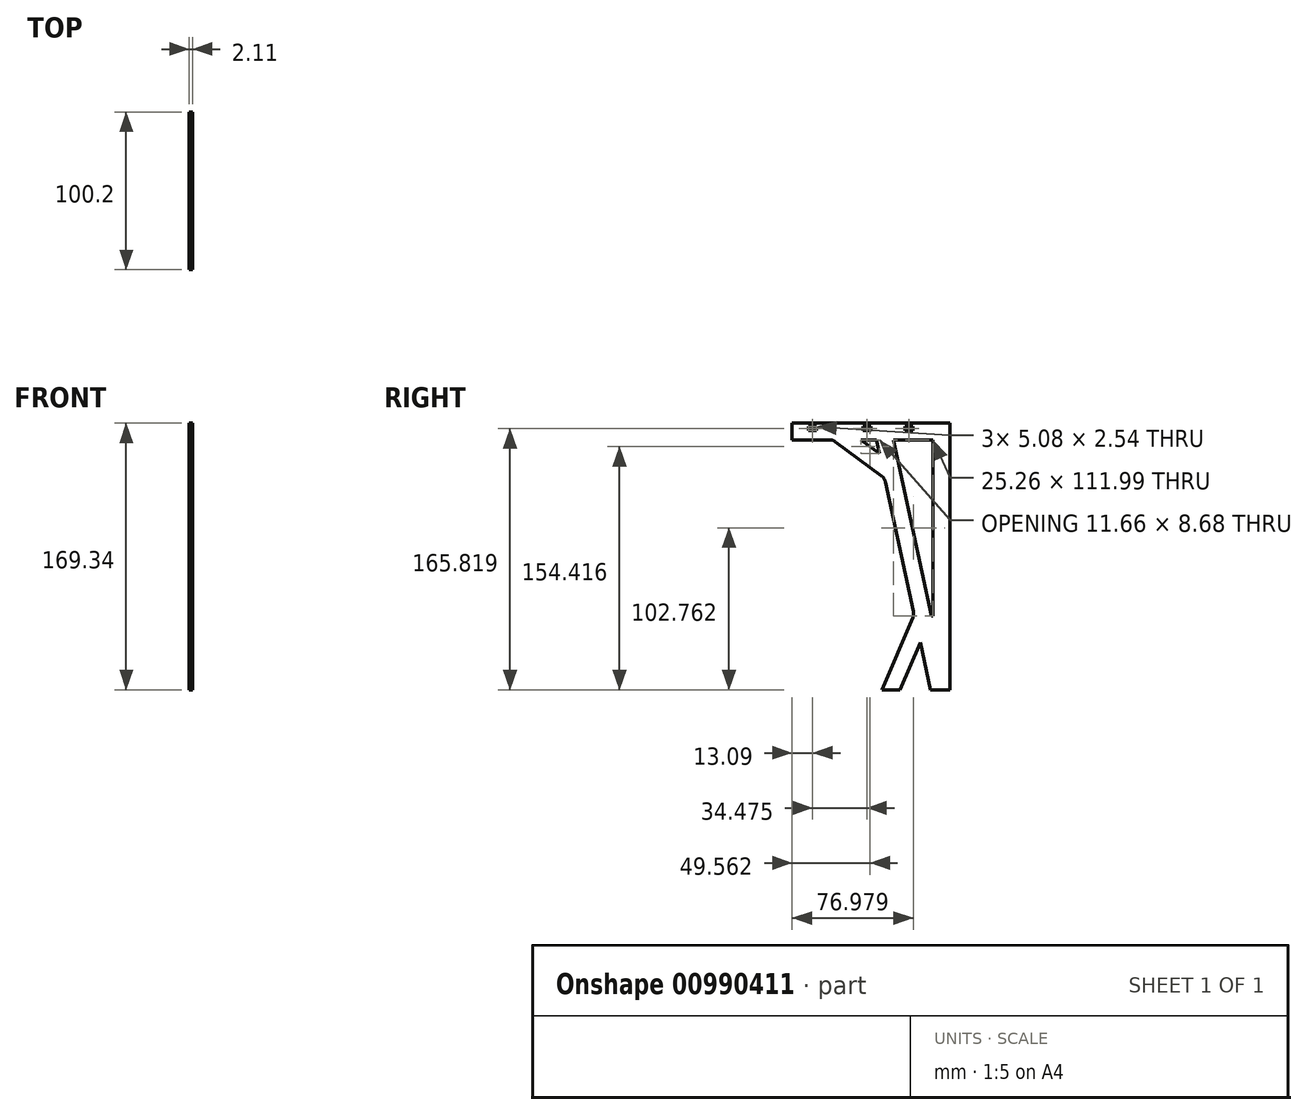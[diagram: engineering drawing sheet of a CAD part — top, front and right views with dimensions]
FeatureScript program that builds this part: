
annotation { "Feature Type Name" : "Feature", "Feature Type Description" : "" }
export const myFeature = defineFeature(function(context is Context, id is Id, definition is map)
    precondition{}
    {
        {
            var Q0;
            Q0=qCreatedBy(makeId("Right.planeOp"),FACE);
            var sketch = newSketch(context, id + "F0", { "sketchPlane" : qUnion([Q0])});
            skLineSegment(sketch, "E0", {"start": v(0, 0) * mm, "end": v(0, 169.34) * mm});
            skLineSegment(sketch, "E1", {"start": v(0, 169.34) * mm, "end": v(200.4, 169.34) * mm});
            skLineSegment(sketch, "E2", {"start": v(0, 0) * mm, "end": v(43.05, 0) * mm, "construction": true});
            skLineSegment(sketch, "E3", {"start": v(43.05, 0) * mm, "end": v(23.47, 45.96) * mm});
            skLineSegment(sketch, "E4", {"start": v(0, 47.82) * mm, "end": v(22.68, 47.82) * mm, "construction": true});
            skLineSegment(sketch, "E5", {"start": v(22.68, 47.82) * mm, "end": v(22.68, 0) * mm, "construction": true});
            skLineSegment(sketch, "E6", {"start": v(23.1, 49.8) * mm, "end": v(40.9, 132) * mm});
            skLineSegment(sketch, "E7", {"start": v(41.4, 134.33) * mm, "end": v(0, 134.33) * mm, "construction": true});
            skLineSegment(sketch, "E8", {"start": v(41.4, 134.33) * mm, "end": v(43.05, 0) * mm, "construction": true});
            skLineSegment(sketch, "E9", {"start": v(43.31, 135.75) * mm, "end": v(72.51, 157.5) * mm});
            skLineSegment(sketch, "E10", {"start": v(74.2, 158.76) * mm, "end": v(74.2, 169.34) * mm, "construction": true});
            skLineSegment(sketch, "E11", {"start": v(74.2, 158.76) * mm, "end": v(0, 158.76) * mm, "construction": true});
            skPoint(sketch, "E12", {"position": v(100.2, 169.34) * mm});
            skLineSegment(sketch, "E13", {"start": v(100.2, 169.34) * mm, "end": v(100.2, 154.3) * mm, "construction": true});
            skLineSegment(sketch, "E14", {"start": v(76.3, 158.76) * mm, "end": v(100.2, 158.76) * mm});
            skLineSegment(sketch, "E15.4", {"start": v(41.18, -0.8) * mm, "end": v(20.56, 47.62) * mm, "construction": true});
            skLineSegment(sketch, "E15.5", {"start": v(20.56, 47.62) * mm, "end": v(39.58, 135.5) * mm});
            skLineSegment(sketch, "E15.6", {"start": v(39.58, 135.5) * mm, "end": v(73.52, 160.79) * mm});
            skLineSegment(sketch, "E15.7", {"start": v(73.52, 160.79) * mm, "end": v(100.2, 160.79) * mm});
            skLineSegment(sketch, "E16.5", {"start": v(11.62, 46.77) * mm, "end": v(31.89, 140.45) * mm});
            skLineSegment(sketch, "E16.6", {"start": v(31.89, 140.45) * mm, "end": v(70.69, 169.35) * mm, "construction": true});
            skLineSegment(sketch, "E16.7", {"start": v(70.69, 169.35) * mm, "end": v(100.2, 169.35) * mm});
            skLineSegment(sketch, "E17", {"start": v(31.89, 140.45) * mm, "end": v(38.14, 169.34) * mm, "construction": true});
            skLineSegment(sketch, "E18", {"start": v(10.6, 158.76) * mm, "end": v(0, 158.76) * mm, "construction": true});
            skLineSegment(sketch, "E19", {"start": v(10.6, 158.76) * mm, "end": v(10.6, 46.77) * mm});
            skLineSegment(sketch, "E20", {"start": v(10.6, 46.77) * mm, "end": v(11.62, 46.77) * mm});
            skLineSegment(sketch, "E21", {"start": v(36.3, 160.79) * mm, "end": v(31.89, 140.45) * mm, "construction": true});
            skLineSegment(sketch, "E22", {"start": v(41.4, 134.33) * mm, "end": v(48.98, 169.34) * mm, "construction": true});
            skLineSegment(sketch, "E23", {"start": v(47.13, 160.79) * mm, "end": v(44.8, 150.07) * mm});
            skLineSegment(sketch, "E24", {"start": v(13.2, 0) * mm, "end": v(0, 0) * mm});
            skLineSegment(sketch, "E25", {"start": v(31.54, 0) * mm, "end": v(43.05, 0) * mm});
            skLineSegment(sketch, "E26", {"start": v(100.2, 158.76) * mm, "end": v(100.2, 169.35) * mm});
            skPoint(sketch, "E27", {"position": v(46.69, 158.76) * mm});
            skPoint(sketch, "E28", {"position": v(56.47, 158.76) * mm});
            skLineSegment(sketch, "E29", {"start": v(46.69, 158.76) * mm, "end": v(56.47, 158.76) * mm});
            skLineSegment(sketch, "E30", {"start": v(44.8, 150.07) * mm, "end": v(46.69, 158.76) * mm});
            skLineSegment(sketch, "E31", {"start": v(10.6, 158.76) * mm, "end": v(35.85, 158.76) * mm});
            skLineSegment(sketch, "E32", {"start": v(35.85, 158.76) * mm, "end": v(31.89, 140.45) * mm});
            skLineSegment(sketch, "E33", {"start": v(44.8, 150.07) * mm, "end": v(56.47, 158.76) * mm});
            skLineSegment(sketch, "E34", {"start": v(30.88, 85.7) * mm, "end": v(20.53, 87.94) * mm, "construction": true});
            skLineSegment(sketch, "E35.0", {"start": v(33.3, -4.15) * mm, "end": v(12.94, 43.67) * mm, "construction": true});
            skLineSegment(sketch, "E36", {"start": v(22.68, 47.82) * mm, "end": v(18.8, 29.9) * mm, "construction": true});
            skLineSegment(sketch, "E37", {"start": v(18.8, 29.9) * mm, "end": v(12.34, 0) * mm});
            skLineSegment(sketch, "E38", {"start": v(18.8, 29.9) * mm, "end": v(31.54, 0) * mm});
            skLineSegment(sketch, "E39", {"start": v(12.34, 0) * mm, "end": v(31.54, 0) * mm});
            skLineSegment(sketch, "E40", {"start": v(20.56, 47.62) * mm, "end": v(40.84, 0) * mm});
            skPoint(sketch, "E41.visualSharp", {"position": v(41.4, 134.33) * mm});
            skArc(sketch, "E41.filletArc", {"start": v(43.31, 135.75) * mm, "mid": v(41.77, 134.1) * mm, "end": v(40.9, 132) * mm});
            skPoint(sketch, "E42.visualSharp", {"position": v(22.68, 47.82) * mm});
            skArc(sketch, "E42.filletArc", {"start": v(23.1, 49.8) * mm, "mid": v(23, 47.85) * mm, "end": v(23.47, 45.96) * mm});
            skPoint(sketch, "E43.visualSharp", {"position": v(74.2, 158.76) * mm});
            skArc(sketch, "E43.filletArc", {"start": v(76.3, 158.76) * mm, "mid": v(74.3, 158.44) * mm, "end": v(72.51, 157.5) * mm});
            skPoint(sketch, "E44", {"position": v(21.75, 93.6) * mm});
            skLineSegment(sketch, "E45", {"start": v(21.75, 93.6) * mm, "end": v(22.1, 95.21) * mm});
            skLineSegment(sketch, "E46", {"start": v(22.1, 95.21) * mm, "end": v(26.54, 94.25) * mm});
            skLineSegment(sketch, "E47", {"start": v(29.56, 96.2) * mm, "end": v(37.5, 132.86) * mm});
            skLineSegment(sketch, "E48", {"start": v(35.55, 135.88) * mm, "end": v(31.1, 136.84) * mm});
            skPoint(sketch, "E49.visualSharp", {"position": v(38.03, 135.35) * mm});
            skArc(sketch, "E49.filletArc", {"start": v(37.5, 132.86) * mm, "mid": v(37.15, 134.78) * mm, "end": v(35.55, 135.88) * mm});
            skPoint(sketch, "E50.visualSharp", {"position": v(29.02, 93.72) * mm});
            skArc(sketch, "E50.filletArc", {"start": v(26.54, 94.25) * mm, "mid": v(28.45, 94.6) * mm, "end": v(29.56, 96.2) * mm});
            skLineSegment(sketch, "E51", {"start": v(21.75, 93.6) * mm, "end": v(32.1, 91.37) * mm, "construction": true});
            skLineSegment(sketch, "E52.0", {"start": v(35.01, 133.4) * mm, "end": v(30.57, 134.36) * mm});
            skLineSegment(sketch, "E52.1", {"start": v(22.64, 97.7) * mm, "end": v(27.08, 96.74) * mm});
            skLineSegment(sketch, "E52.2", {"start": v(27.08, 96.74) * mm, "end": v(27.08, 96.74) * mm});
            skLineSegment(sketch, "E52.3", {"start": v(27.08, 96.74) * mm, "end": v(35.01, 133.4) * mm});
            skLineSegment(sketch, "E52.4", {"start": v(35.01, 133.4) * mm, "end": v(35.01, 133.4) * mm});
            skLineSegment(sketch, "E53.MirrorCS", {"start": v(21.4, 92) * mm, "end": v(25.85, 91.04) * mm});
            skArc(sketch, "E54.MirrorCS", {"start": v(25.85, 91.04) * mm, "mid": v(27.44, 89.94) * mm, "end": v(27.8, 88.02) * mm});
            skLineSegment(sketch, "E55.MirrorCS", {"start": v(27.8, 88.02) * mm, "end": v(19.86, 51.36) * mm});
            skArc(sketch, "E56.MirrorCS", {"start": v(19.86, 51.36) * mm, "mid": v(18.75, 49.76) * mm, "end": v(16.84, 49.41) * mm});
            skLineSegment(sketch, "E57.MirrorCS", {"start": v(16.84, 49.41) * mm, "end": v(12.4, 50.38) * mm});
            skLineSegment(sketch, "E58.MirrorCS", {"start": v(17.37, 51.9) * mm, "end": v(12.94, 52.86) * mm});
            skLineSegment(sketch, "E59.MirrorCS", {"start": v(25.3, 88.56) * mm, "end": v(17.37, 51.9) * mm});
            skLineSegment(sketch, "E60.MirrorCS", {"start": v(20.87, 89.52) * mm, "end": v(25.3, 88.56) * mm});
            skLineSegment(sketch, "E61", {"start": v(33.72, 127.42) * mm, "end": v(31.23, 127.96) * mm});
            skLineSegment(sketch, "E62", {"start": v(31.23, 127.96) * mm, "end": v(30.16, 123) * mm});
            skLineSegment(sketch, "E63", {"start": v(30.16, 123) * mm, "end": v(32.64, 122.46) * mm});
            skLineSegment(sketch, "E64", {"start": v(28.37, 102.7) * mm, "end": v(25.88, 103.24) * mm});
            skLineSegment(sketch, "E65", {"start": v(25.88, 103.24) * mm, "end": v(26.96, 108.2) * mm});
            skLineSegment(sketch, "E66", {"start": v(26.96, 108.2) * mm, "end": v(29.44, 107.66) * mm});
            skLineSegment(sketch, "E67.MirrorCS", {"start": v(24.02, 82.6) * mm, "end": v(21.54, 83.13) * mm});
            skLineSegment(sketch, "E68.MirrorCS", {"start": v(21.54, 83.13) * mm, "end": v(20.46, 78.17) * mm});
            skLineSegment(sketch, "E69.MirrorCS", {"start": v(20.46, 78.17) * mm, "end": v(22.94, 77.63) * mm});
            skLineSegment(sketch, "E70.MirrorCS", {"start": v(17.26, 63.37) * mm, "end": v(19.74, 62.84) * mm});
            skLineSegment(sketch, "E71.MirrorCS", {"start": v(16.19, 58.4) * mm, "end": v(17.26, 63.37) * mm});
            skLineSegment(sketch, "E72.MirrorCS", {"start": v(18.67, 57.87) * mm, "end": v(16.19, 58.4) * mm});
            skLineSegment(sketch, "E73", {"start": v(31.89, 140.45) * mm, "end": v(41.4, 134.33) * mm, "construction": true});
            skLineSegment(sketch, "E74.MirrorCS", {"start": v(37.56, 139.02) * mm, "end": v(34.85, 142.66) * mm});
            skArc(sketch, "E75.MirrorCS", {"start": v(41.12, 138.5) * mm, "mid": v(39.23, 138.02) * mm, "end": v(37.56, 139.02) * mm});
            skLineSegment(sketch, "E76.MirrorCS", {"start": v(71.2, 160.9) * mm, "end": v(41.12, 138.5) * mm});
            skArc(sketch, "E77.MirrorCS", {"start": v(71.72, 164.46) * mm, "mid": v(72.2, 162.57) * mm, "end": v(71.2, 160.9) * mm});
            skLineSegment(sketch, "E78.MirrorCS", {"start": v(69, 168.1) * mm, "end": v(71.72, 164.46) * mm});
            skLineSegment(sketch, "E79.MirrorCS", {"start": v(66.97, 166.58) * mm, "end": v(69.69, 162.94) * mm});
            skLineSegment(sketch, "E80.MirrorCS", {"start": v(69.69, 162.94) * mm, "end": v(39.6, 140.53) * mm});
            skLineSegment(sketch, "E81.MirrorCS", {"start": v(64.8, 159.3) * mm, "end": v(63.28, 161.33) * mm});
            skLineSegment(sketch, "E82.MirrorCS", {"start": v(63.28, 161.33) * mm, "end": v(59.2, 158.3) * mm});
            skLineSegment(sketch, "E83.MirrorCS", {"start": v(59.2, 158.3) * mm, "end": v(60.72, 156.26) * mm});
            skLineSegment(sketch, "E84.MirrorCS", {"start": v(47.06, 149.26) * mm, "end": v(48.58, 147.22) * mm});
            skLineSegment(sketch, "E85.MirrorCS", {"start": v(42.99, 146.22) * mm, "end": v(47.06, 149.26) * mm});
            skLineSegment(sketch, "E86.MirrorCS", {"start": v(44.5, 144.19) * mm, "end": v(42.99, 146.22) * mm});
            skLineSegment(sketch, "E87.MirrorCS", {"start": v(39.6, 140.53) * mm, "end": v(36.89, 144.18) * mm});
            skLineSegment(sketch, "E88", {"start": v(70.69, 169.35) * mm, "end": v(70.69, 164.55) * mm});
            skPoint(sketch, "E89.visualSharp", {"position": v(70.69, 162) * mm});
            skArc(sketch, "E89.filletArc", {"start": v(68.15, 162) * mm, "mid": v(69.94, 162.75) * mm, "end": v(70.69, 164.55) * mm});
            skLineSegment(sketch, "E90.1", {"start": v(68.15, 169.63) * mm, "end": v(68.15, 164.55) * mm});
            skLineSegment(sketch, "E91", {"start": v(55.17, 164.55) * mm, "end": v(55.17, 167.09) * mm});
            skLineSegment(sketch, "E92", {"start": v(55.17, 167.09) * mm, "end": v(50.1, 167.09) * mm});
            skLineSegment(sketch, "E93", {"start": v(50.1, 167.09) * mm, "end": v(50.1, 164.55) * mm});
            skLineSegment(sketch, "E94", {"start": v(28.37, 164.55) * mm, "end": v(28.37, 167.09) * mm});
            skLineSegment(sketch, "E95", {"start": v(28.37, 167.09) * mm, "end": v(23.3, 167.09) * mm});
            skLineSegment(sketch, "E96", {"start": v(23.3, 167.09) * mm, "end": v(23.3, 164.55) * mm});
            skLineSegment(sketch, "E97", {"start": v(22.68, 47.82) * mm, "end": v(11.62, 46.77) * mm, "construction": true});
            skLineSegment(sketch, "E98", {"start": v(15.36, 37.97) * mm, "end": v(19.78, 39.85) * mm});
            skLineSegment(sketch, "E99", {"start": v(23.11, 38.51) * mm, "end": v(37.3, 5.2) * mm});
            skLineSegment(sketch, "E100", {"start": v(35.96, 1.87) * mm, "end": v(31.54, -0.01) * mm});
            skPoint(sketch, "E101.visualSharp", {"position": v(38.3, 2.87) * mm});
            skArc(sketch, "E101.filletArc", {"start": v(35.96, 1.87) * mm, "mid": v(37.32, 3.26) * mm, "end": v(37.3, 5.2) * mm});
            skPoint(sketch, "E102.visualSharp", {"position": v(22.12, 40.85) * mm});
            skArc(sketch, "E102.filletArc", {"start": v(23.11, 38.51) * mm, "mid": v(21.72, 39.87) * mm, "end": v(19.78, 39.85) * mm});
            skLineSegment(sketch, "E103.0", {"start": v(34.97, 4.2) * mm, "end": v(25.52, 0.18) * mm});
            skLineSegment(sketch, "E103.1", {"start": v(20.78, 37.52) * mm, "end": v(34.97, 4.2) * mm});
            skLineSegment(sketch, "E103.2", {"start": v(16.36, 35.63) * mm, "end": v(20.78, 37.52) * mm});
            skLineSegment(sketch, "E104", {"start": v(27.86, 20.9) * mm, "end": v(25.52, 19.9) * mm});
            skLineSegment(sketch, "E105", {"start": v(25.52, 19.9) * mm, "end": v(23.53, 24.57) * mm});
            skLineSegment(sketch, "E106", {"start": v(23.53, 24.57) * mm, "end": v(25.87, 25.57) * mm});
            skLineSegment(sketch, "E107", {"start": v(21.48, 35.85) * mm, "end": v(19.15, 34.86) * mm});
            skLineSegment(sketch, "E108", {"start": v(19.15, 34.86) * mm, "end": v(21.14, 30.18) * mm});
            skLineSegment(sketch, "E109", {"start": v(21.14, 30.18) * mm, "end": v(23.48, 31.18) * mm});
            skLineSegment(sketch, "E110", {"start": v(79.6, 169.35) * mm, "end": v(79.6, 164.55) * mm});
            skLineSegment(sketch, "E111", {"start": v(82.14, 162) * mm, "end": v(100.2, 162) * mm});
            skPoint(sketch, "E112.visualSharp", {"position": v(79.6, 162) * mm});
            skArc(sketch, "E112.filletArc", {"start": v(79.6, 164.55) * mm, "mid": v(80.34, 162.75) * mm, "end": v(82.14, 162) * mm});
            skLineSegment(sketch, "E113.0", {"start": v(82.14, 164.55) * mm, "end": v(100.2, 164.55) * mm});
            skLineSegment(sketch, "E113.1", {"start": v(82.14, 169.35) * mm, "end": v(82.14, 164.55) * mm});
            skLineSegment(sketch, "E114", {"start": v(84.57, 164.55) * mm, "end": v(84.57, 167.09) * mm});
            skPoint(sketch, "E114.endSnap0", {"position": v(68.15, 167.09) * mm});
            skLineSegment(sketch, "E115", {"start": v(84.57, 167.09) * mm, "end": v(89.65, 167.09) * mm});
            skLineSegment(sketch, "E116", {"start": v(89.65, 167.09) * mm, "end": v(89.65, 164.55) * mm});
            skLineSegment(sketch, "E117", {"start": v(10.6, 158.76) * mm, "end": v(10.6, 164.55) * mm, "construction": true});
            skLineSegment(sketch, "E118", {"start": v(68.15, 164.55) * mm, "end": v(18.21, 164.55) * mm});
            skLineSegment(sketch, "E119", {"start": v(68.15, 162) * mm, "end": v(18.21, 162) * mm});
            skLineSegment(sketch, "E120", {"start": v(18.21, 164.55) * mm, "end": v(18.21, 169.34) * mm});
            skLineSegment(sketch, "E121", {"start": v(15.67, 164.55) * mm, "end": v(15.67, 169.34) * mm});
            skPoint(sketch, "E122.visualSharp", {"position": v(15.67, 162) * mm});
            skArc(sketch, "E122.filletArc", {"start": v(15.67, 164.55) * mm, "mid": v(16.42, 162.75) * mm, "end": v(18.21, 162) * mm});
            skLineSegment(sketch, "E123", {"start": v(15.67, 164.55) * mm, "end": v(18.21, 164.55) * mm, "construction": true});
            skLineSegment(sketch, "E124", {"start": v(10.6, 164.55) * mm, "end": v(15.67, 164.55) * mm, "construction": true});
            skLineSegment(sketch, "E125", {"start": v(23.3, 165.82) * mm, "end": v(18.21, 165.82) * mm, "construction": true});
            skSolve(sketch);
        }
        {
            var Q0;
            Q0=makeQuery(id+"F0.imprint","IMPRINT",FACE,{"disambiguationData":[TD([[makeQuery(id+"F0.imprint","IMPRINT",EDGE,{"derivedFrom":sQuery(id+"F0.wireOp",EDGE,"E15.5")}),1.0]])]});
            var Q1;
            {var subQ0=sQuery(id+"F0.wireOp",EDGE,"E91");Q1=makeQuery(id+"F0.imprint","IMPRINT",FACE,{"disambiguationData":[TD([[makeQuery(id+"F0.imprint","IMPRINT",EDGE,{"derivedFrom":subQ0}),-1.0]])]});}
            var Q2;
            {var subQ10=sQuery(id+"F0.wireOp",EDGE,"Y5XbKFPJ-2wYX-9icL-y4mU-RIpAKNCXkipD");Q2=makeQuery(id+"F0.imprint","IMPRINT",FACE,{"disambiguationData":[TD([[makeQuery(id+"F0.imprint","IMPRINT",EDGE,{"derivedFrom":subQ10}),-1.0]])]});}
            var Q3;
            {var subQ0=sQuery(id+"F0.wireOp",EDGE,"E84.MirrorCS");Q3=makeQuery(id+"F0.imprint","IMPRINT",FACE,{"disambiguationData":[TD([[makeQuery(id+"F0.imprint","IMPRINT",EDGE,{"derivedFrom":subQ0}),-1.0]])]});}
            var Q4;
            {var subQ0=sQuery(id+"F0.wireOp",EDGE,"E81.MirrorCS");Q4=makeQuery(id+"F0.imprint","IMPRINT",FACE,{"disambiguationData":[TD([[makeQuery(id+"F0.imprint","IMPRINT",EDGE,{"derivedFrom":subQ0}),1.0]])]});}
            var Q5;
            {var subQ0=sQuery(id+"F0.wireOp",EDGE,"E88");var subQ1=makeQuery(id+"F0.imprint","IMPRINT",VERTEX,{"derivedFrom":subQ0});Q5=makeQuery(id+"F0.imprint","IMPRINT",FACE,{"disambiguationData":[TD([[makeQuery(id+"F0.imprint","IMPRINT",EDGE,{"disambiguationData":[TD([[subQ1,1.0]])],"derivedFrom":subQ0}),-1.0]])]});}
            var Q6;
            {var subQ3=sQuery(id+"F0.wireOp",EDGE,"E114");Q6=makeQuery(id+"F0.imprint","IMPRINT",FACE,{"disambiguationData":[TD([[makeQuery(id+"F0.imprint","IMPRINT",EDGE,{"derivedFrom":subQ3}),1.0]])]});}
            var Q7;
            {var subQ4=sQuery(id+"F0.wireOp",EDGE,"E111");Q7=makeQuery(id+"F0.imprint","IMPRINT",FACE,{"disambiguationData":[TD([[makeQuery(id+"F0.imprint","IMPRINT",EDGE,{"derivedFrom":subQ4}),1.0]])]});}
            var Q8;
            {var subQ2=sQuery(id+"F0.wireOp",EDGE,"E3");Q8=makeQuery(id+"F0.imprint","IMPRINT",FACE,{"disambiguationData":[TD([[makeQuery(id+"F0.imprint","IMPRINT",EDGE,{"derivedFrom":subQ2}),1.0]])]});}
            var Q9;
            {var subQ5=sQuery(id+"F0.wireOp",EDGE,"E46");Q9=makeQuery(id+"F0.imprint","IMPRINT",FACE,{"disambiguationData":[TD([[makeQuery(id+"F0.imprint","IMPRINT",EDGE,{"derivedFrom":subQ5}),1.0]])]});}
            var Q10;
            {var subQ3=sQuery(id+"F0.wireOp",EDGE,"E52.0");Q10=makeQuery(id+"F0.imprint","IMPRINT",FACE,{"disambiguationData":[TD([[makeQuery(id+"F0.imprint","IMPRINT",EDGE,{"derivedFrom":subQ3}),1.0]])]});}
            var Q11;
            {var subQ0=sQuery(id+"F0.wireOp",EDGE,"E61");Q11=makeQuery(id+"F0.imprint","IMPRINT",FACE,{"disambiguationData":[TD([[makeQuery(id+"F0.imprint","IMPRINT",EDGE,{"derivedFrom":subQ0}),1.0]])]});}
            var Q12;
            {var subQ0=sQuery(id+"F0.wireOp",EDGE,"E64");Q12=makeQuery(id+"F0.imprint","IMPRINT",FACE,{"disambiguationData":[TD([[makeQuery(id+"F0.imprint","IMPRINT",EDGE,{"derivedFrom":subQ0}),-1.0]])]});}
            var Q13;
            {var subQ7=sQuery(id+"F0.wireOp",EDGE,"E53.MirrorCS");Q13=makeQuery(id+"F0.imprint","IMPRINT",FACE,{"disambiguationData":[TD([[makeQuery(id+"F0.imprint","IMPRINT",EDGE,{"derivedFrom":subQ7}),-1.0]])]});}
            var Q14;
            {var subQ0=sQuery(id+"F0.wireOp",EDGE,"E67.MirrorCS");Q14=makeQuery(id+"F0.imprint","IMPRINT",FACE,{"disambiguationData":[TD([[makeQuery(id+"F0.imprint","IMPRINT",EDGE,{"derivedFrom":subQ0}),1.0]])]});}
            var Q15;
            {var subQ4=sQuery(id+"F0.wireOp",EDGE,"E58.MirrorCS");Q15=makeQuery(id+"F0.imprint","IMPRINT",FACE,{"disambiguationData":[TD([[makeQuery(id+"F0.imprint","IMPRINT",EDGE,{"derivedFrom":subQ4}),-1.0]])]});}
            var Q16;
            {var subQ0=sQuery(id+"F0.wireOp",EDGE,"E70.MirrorCS");Q16=makeQuery(id+"F0.imprint","IMPRINT",FACE,{"disambiguationData":[TD([[makeQuery(id+"F0.imprint","IMPRINT",EDGE,{"derivedFrom":subQ0}),-1.0]])]});}
            var Q17;
            {var subQ0=sQuery(id+"F0.wireOp",EDGE,"E107");Q17=makeQuery(id+"F0.imprint","IMPRINT",FACE,{"disambiguationData":[TD([[makeQuery(id+"F0.imprint","IMPRINT",EDGE,{"derivedFrom":subQ0}),1.0]])]});}
            var Q18;
            {var subQ0=sQuery(id+"F0.wireOp",EDGE,"E104");Q18=makeQuery(id+"F0.imprint","IMPRINT",FACE,{"disambiguationData":[TD([[makeQuery(id+"F0.imprint","IMPRINT",EDGE,{"derivedFrom":subQ0}),-1.0]])]});}
            var Q19;
            {var subQ16=sQuery(id+"F0.wireOp",EDGE,"E119");Q19=makeQuery(id+"F0.imprint","IMPRINT",FACE,{"disambiguationData":[TD([[makeQuery(id+"F0.imprint","IMPRINT",EDGE,{"derivedFrom":subQ16}),-1.0]])]});}
            extrude(context, id + "F1", {"entities" : qUnion([Q0, Q1, Q2, Q3, Q4, Q5, Q6, Q7, Q8, Q9, Q10, Q11, Q12, Q13, Q14, Q15, Q16, Q17, Q18, Q19]), "depth" : 2.1 * mm, "offsetDistance" : 25.4 * mm});
        }
        {
            var Q0;
            Q0=makeQuery(id+"F1.opExtrude","CAP_EDGE",EDGE,{"disambiguationData":[OSD([sQuery(id+"F0.wireOp",EDGE,"E6")])],"isStart":false});
            fillet(context, id + "F2", {"entities" : qUnion([Q0]), "radius" : 0.76 * mm, "tangentPropagation" : true, "allowEdgeOverflow" : false});
        }
        {
            var Q0;
            Q0=makeQuery(id+"F1.opExtrude","SWEPT_BODY",BODY,{"disambiguationData":[OSD([sQuery(id+"F0.wireOp",EDGE,"E0"),sQuery(id+"F0.wireOp",EDGE,"E1"),sQuery(id+"F0.wireOp",EDGE,"E3"),sQuery(id+"F0.wireOp",EDGE,"E6"),sQuery(id+"F0.wireOp",EDGE,"E9"),sQuery(id+"F0.wireOp",EDGE,"E14"),sQuery(id+"F0.wireOp",EDGE,"E16.5"),sQuery(id+"F0.wireOp",EDGE,"E19"),sQuery(id+"F0.wireOp",EDGE,"E20"),sQuery(id+"F0.wireOp",EDGE,"E24"),sQuery(id+"F0.wireOp",EDGE,"E25"),sQuery(id+"F0.wireOp",EDGE,"E26"),sQuery(id+"F0.wireOp",EDGE,"E29"),sQuery(id+"F0.wireOp",EDGE,"E30"),sQuery(id+"F0.wireOp",EDGE,"E31"),sQuery(id+"F0.wireOp",EDGE,"E32"),sQuery(id+"F0.wireOp",EDGE,"E33"),sQuery(id+"F0.wireOp",EDGE,"E37"),sQuery(id+"F0.wireOp",EDGE,"E38"),sQuery(id+"F0.wireOp",EDGE,"E41.filletArc"),sQuery(id+"F0.wireOp",EDGE,"E42.filletArc"),sQuery(id+"F0.wireOp",EDGE,"E43.filletArc"),sQuery(id+"F0.wireOp",EDGE,"E45"),sQuery(id+"F0.wireOp",EDGE,"E91"),sQuery(id+"F0.wireOp",EDGE,"E92"),sQuery(id+"F0.wireOp",EDGE,"E93"),sQuery(id+"F0.wireOp",EDGE,"E94"),sQuery(id+"F0.wireOp",EDGE,"E95"),sQuery(id+"F0.wireOp",EDGE,"E96"),sQuery(id+"F0.wireOp",EDGE,"E113.0"),sQuery(id+"F0.wireOp",EDGE,"E114"),sQuery(id+"F0.wireOp",EDGE,"E115"),sQuery(id+"F0.wireOp",EDGE,"E116"),sQuery(id+"F0.wireOp",EDGE,"E118")])]});
            var Q1;
            Q1=sQuery(id+"F0.wireOp",EDGE,"E0");
            transform(context, id + "F3", {"entities" : qUnion([Q0]), "transformType" : TransformType.ROTATION, "transformAxis" : qUnion([Q1]), "angle" : 180 * degree, "makeCopy" : false});
        }
    });
